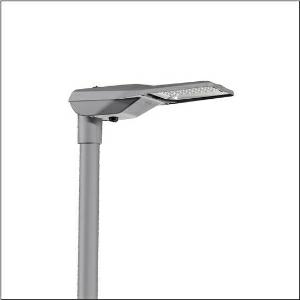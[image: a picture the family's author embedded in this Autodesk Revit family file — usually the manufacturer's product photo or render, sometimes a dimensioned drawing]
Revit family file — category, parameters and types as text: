
# Revit family: streetlight_sl_21_mini___stw1_0a_5xe2e33t08gb_f20d
name_source: partatom
category: Lighting Fixtures
units: mm (PartAtom-declared; Revit-internal decimal feet)

## family parameters
Cut with Voids When Loaded = No
Host = Face
Light Source = No
Part Type = Normal
Room Calculation Point = No
Round Connector Dimension = Use Diameter
Shared = No

## types (1)
- --- (1 x LED, 5940 lm, 40.4 W, 3000K)
    Apparent Load = 40 VA
    CIE Flux Codes = 38 75 98 100 100
    Color Rendering = 70
    Color Temperature = 3000K
    Default Elevation = 1800 mm
    Description = Streetlight SL 21 mini, mast luminaire, primary light control with lens, of PMMA, primary optical cover: cover, of toughened safety glass, transparent, light distribution: STW1.0a, light emission: direct distribution, primary light characteristic: asymmetric, installation type: side-entry, post-top, LED, High Power LED, rated luminous flux: 5.940lm, luminous efficacy: 147lm/W, light colour: 730, colour temperature: 3000K, control gear: D4i, control: overheat protection, constant luminous flux control, time-dependent luminous flux control, flexible luminous flux parameterisation, pre-setting: logarithmic dimming characteristic, mains connection: 220..240V, AC, 50/60Hz, start of lifetime: 40W, end of service life: 41W, reduction: 19W, luminaire housing, of diecast aluminium, powder-coated, Siteco® metallic grey (DB 702S), corrosivity category C5 mid according to DIN EN ISO 12944, please order mast flange separately, inclination adjustable: 0°, 5°, 10°, 15°, sealing non-destructively replaceable, multi-level sealing system, length: 628mm, width: 235mm, height: 110mm, mast flange for spigot size: 42mm (side-entry): 5XC10008XM4, 60/48mm (side-entry/post-top): 5XC10108XM2, 76/60mm (side-entry/post-top): 5XC10108XM1, mounting height: 4..8m, Smart Interface below and above, protection rating (complete): IP66, insulation class (complete): insulation class II (safety insulation), certification: CE, ENEC, ENEC+, VDE, impact resistance: IK10, permissible operating ambient temperature for outdoor applications: -40..+50°C, standard-compliant lighting for roads and squares, packaging unit: 1 piece

Light Distribution: STW1.0a
    Height = 110 mm
    Lamp = 1 x LED
    Lamp Light Flux = 5940 lm
    Lamp Power = 40.4 W
    Lamp count = 1
    Length = 625 mm
    Luminous efficacy = 147 lm/W
    Manufacturer = Siteco
    ModVariant = No
    Model = 5XE2E33T08GB
    Number of Poles = 1
    OnlyDefault = Yes
    Power Factor = 1
    Product Name = Streetlight SL 21 mini | STW1.0a
    Product group = mast luminaire | pylon top
    ProductGroupID = 6100
    Protection Class = Protection class II
    Protection Degree = IP 66
    RLX_Detail_Level = 1
    RLX_Emergency_Light_Flux = 0 lm
    RLX_Emergency_Type = 0
    RLX_Emergency_Type_DB = No
    RlxData = <blob elided: 26425 chars, md5=4c6fb888>
    Socket = socket
    Standby Power = 0 W
    System Light Flux = 5940 lm
    System Power = 40 W
    Type Comments = factory setting: luminous flux: 100 % | dim-lin: 254 | 812 mA
    Type Image = l_1003514.jpg
    URL = http://relux.com
    VarID = @adj_187296
    Voltage = 0 V
    Weight = 0.00 kg
    Width = 234 mm

## geometry (parser evidence)
native form markers: Blend x4, Sweep x12
no freeform markers — native parametric forms only
